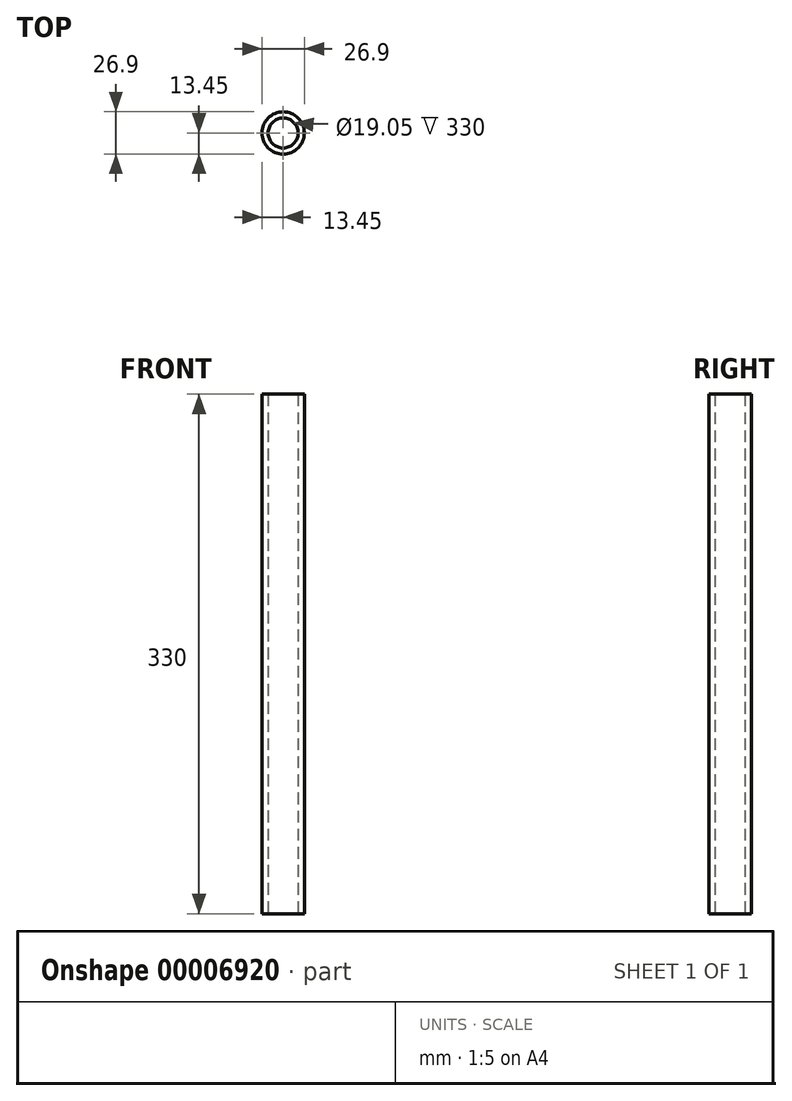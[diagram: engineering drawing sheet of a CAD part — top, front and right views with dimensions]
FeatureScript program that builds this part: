
annotation { "Feature Type Name" : "Feature", "Feature Type Description" : "" }
export const myFeature = defineFeature(function(context is Context, id is Id, definition is map)
    precondition{}
    {
        {
            var Q0;
            Q0=qCreatedBy(makeId("Top.planeOp"),FACE);
            var sketch = newSketch(context, id + "F0", { "sketchPlane" : qUnion([Q0])});
            skCircle(sketch, "E0", {"center": v(0, 0) * mm, "radius": 13.45 * mm});
            skCircle(sketch, "E1", {"center": v(0, 0) * mm, "radius": 9.53 * mm});
            skSolve(sketch);
        }
        {
            var Q0;
            Q0=makeQuery(id+"F0.imprint","IMPRINT",FACE,{"disambiguationData":[TD([[makeQuery(id+"F0.imprint","IMPRINT",EDGE,{"derivedFrom":sQuery(id+"F0.wireOp",EDGE,"E0")}),1.0]])]});
            extrude(context, id + "F1", {"entities" : qUnion([Q0]), "depth" : 330 * mm});
        }
    });
